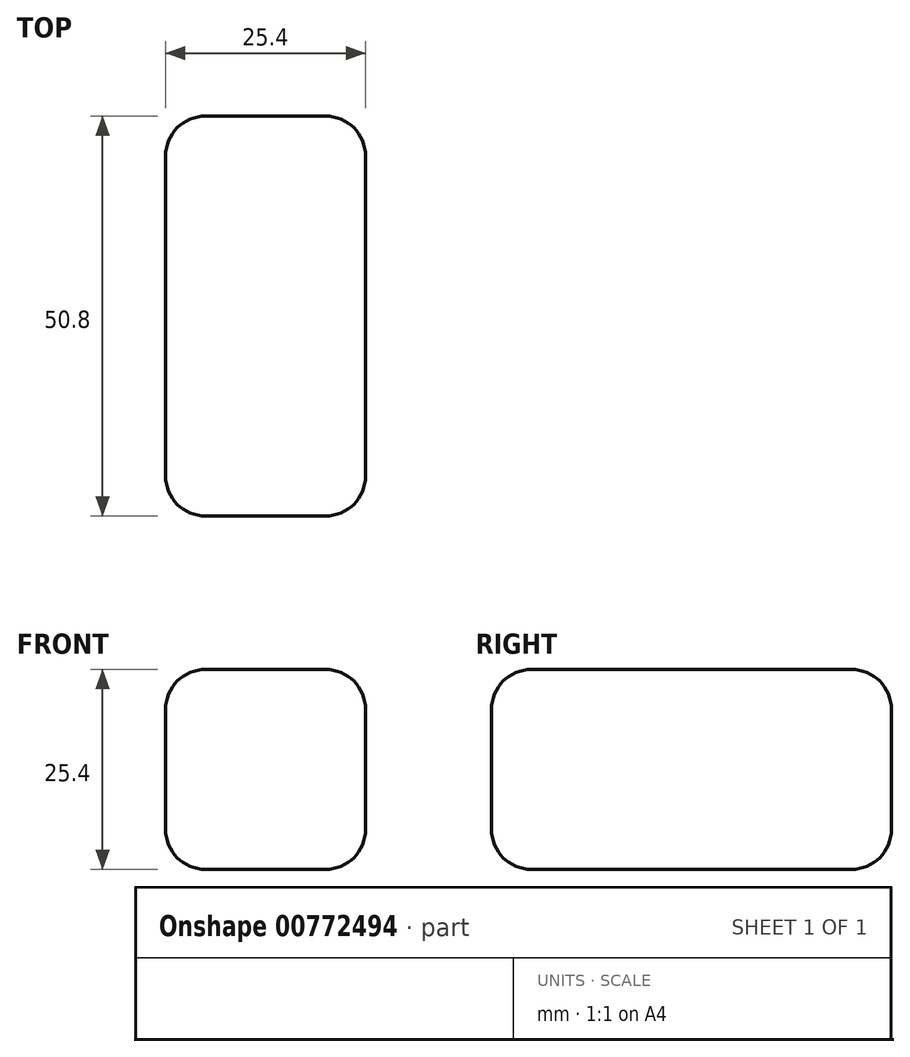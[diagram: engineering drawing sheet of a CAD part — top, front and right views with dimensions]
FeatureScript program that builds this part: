
annotation { "Feature Type Name" : "Feature", "Feature Type Description" : "" }
export const myFeature = defineFeature(function(context is Context, id is Id, definition is map)
    precondition{}
    {
        {
            var Q0;
            Q0=qCreatedBy(makeId("Top.planeOp"),FACE);
            var sketch = newSketch(context, id + "F0", { "sketchPlane" : qUnion([Q0])});
            skLineSegment(sketch, "E0.bottom", {"start": v(12.7, -25.4) * mm, "end": v(-12.7, -25.4) * mm});
            skLineSegment(sketch, "E0.top", {"start": v(12.7, 25.4) * mm, "end": v(-12.7, 25.4) * mm});
            skLineSegment(sketch, "E0.left", {"start": v(12.7, -25.4) * mm, "end": v(12.7, 25.4) * mm});
            skLineSegment(sketch, "E0.right", {"start": v(-12.7, -25.4) * mm, "end": v(-12.7, 25.4) * mm});
            skPoint(sketch, "E0.middle", {"position": v(0, 0) * mm});
            skSolve(sketch);
        }
        {
            var Q0;
            Q0=makeQuery(id+"F0.imprint","IMPRINT",FACE,{"disambiguationData":[TD([[makeQuery(id+"F0.imprint","IMPRINT",EDGE,{"derivedFrom":sQuery(id+"F0.wireOp",EDGE,"E0.bottom")}),-1.0]])]});
            extrude(context, id + "F1", {"entities" : qUnion([Q0]), "depth" : 25.4 * mm, "offsetDistance" : 25.4 * mm});
        }
        {
            var Q0;
            Q0=makeQuery(id+"F1.opExtrude","CAP_EDGE",EDGE,{"disambiguationData":[OSD([sQuery(id+"F0.wireOp",EDGE,"E0.left")])],"isStart":false});
            var Q1;
            Q1=makeQuery(id+"F1.opExtrude","CAP_EDGE",EDGE,{"disambiguationData":[OSD([sQuery(id+"F0.wireOp",EDGE,"E0.right")])],"isStart":false});
            var Q2;
            Q2=makeQuery(id+"F1.opExtrude","SWEPT_EDGE",EDGE,{"disambiguationData":[OSD([sQuery(id+"F0.wireOp",EDGE,"E0.bottom"),sQuery(id+"F0.wireOp",EDGE,"E0.right")])]});
            var Q3;
            Q3=makeQuery(id+"F1.opExtrude","SWEPT_EDGE",EDGE,{"disambiguationData":[OSD([sQuery(id+"F0.wireOp",EDGE,"E0.top"),sQuery(id+"F0.wireOp",EDGE,"E0.left")])]});
            var Q4;
            Q4=makeQuery(id+"F1.opExtrude","SWEPT_EDGE",EDGE,{"disambiguationData":[OSD([sQuery(id+"F0.wireOp",EDGE,"E0.top"),sQuery(id+"F0.wireOp",EDGE,"E0.right")])]});
            var Q5;
            Q5=makeQuery(id+"F1.opExtrude","SWEPT_EDGE",EDGE,{"disambiguationData":[OSD([sQuery(id+"F0.wireOp",EDGE,"E0.bottom"),sQuery(id+"F0.wireOp",EDGE,"E0.left")])]});
            var Q6;
            Q6=makeQuery(id+"F1.opExtrude","CAP_EDGE",EDGE,{"disambiguationData":[OSD([sQuery(id+"F0.wireOp",EDGE,"E0.bottom")])],"isStart":false});
            var Q7;
            Q7=makeQuery(id+"F1.opExtrude","CAP_EDGE",EDGE,{"disambiguationData":[OSD([sQuery(id+"F0.wireOp",EDGE,"E0.top")])],"isStart":false});
            var Q8;
            Q8=makeQuery(id+"F1.opExtrude","CAP_EDGE",EDGE,{"disambiguationData":[OSD([sQuery(id+"F0.wireOp",EDGE,"E0.left")])],"isStart":true});
            var Q9;
            Q9=makeQuery(id+"F1.opExtrude","CAP_EDGE",EDGE,{"disambiguationData":[OSD([sQuery(id+"F0.wireOp",EDGE,"E0.bottom")])],"isStart":true});
            var Q10;
            Q10=makeQuery(id+"F1.opExtrude","CAP_EDGE",EDGE,{"disambiguationData":[OSD([sQuery(id+"F0.wireOp",EDGE,"E0.right")])],"isStart":true});
            var Q11;
            Q11=makeQuery(id+"F1.opExtrude","CAP_EDGE",EDGE,{"disambiguationData":[OSD([sQuery(id+"F0.wireOp",EDGE,"E0.top")])],"isStart":true});
            fillet(context, id + "F2", {"entities" : qUnion([Q0, Q1, Q2, Q3, Q4, Q5, Q6, Q7, Q8, Q9, Q10, Q11]), "radius" : 5.08 * mm, "tangentPropagation" : true, "allowEdgeOverflow" : false});
        }
    });
